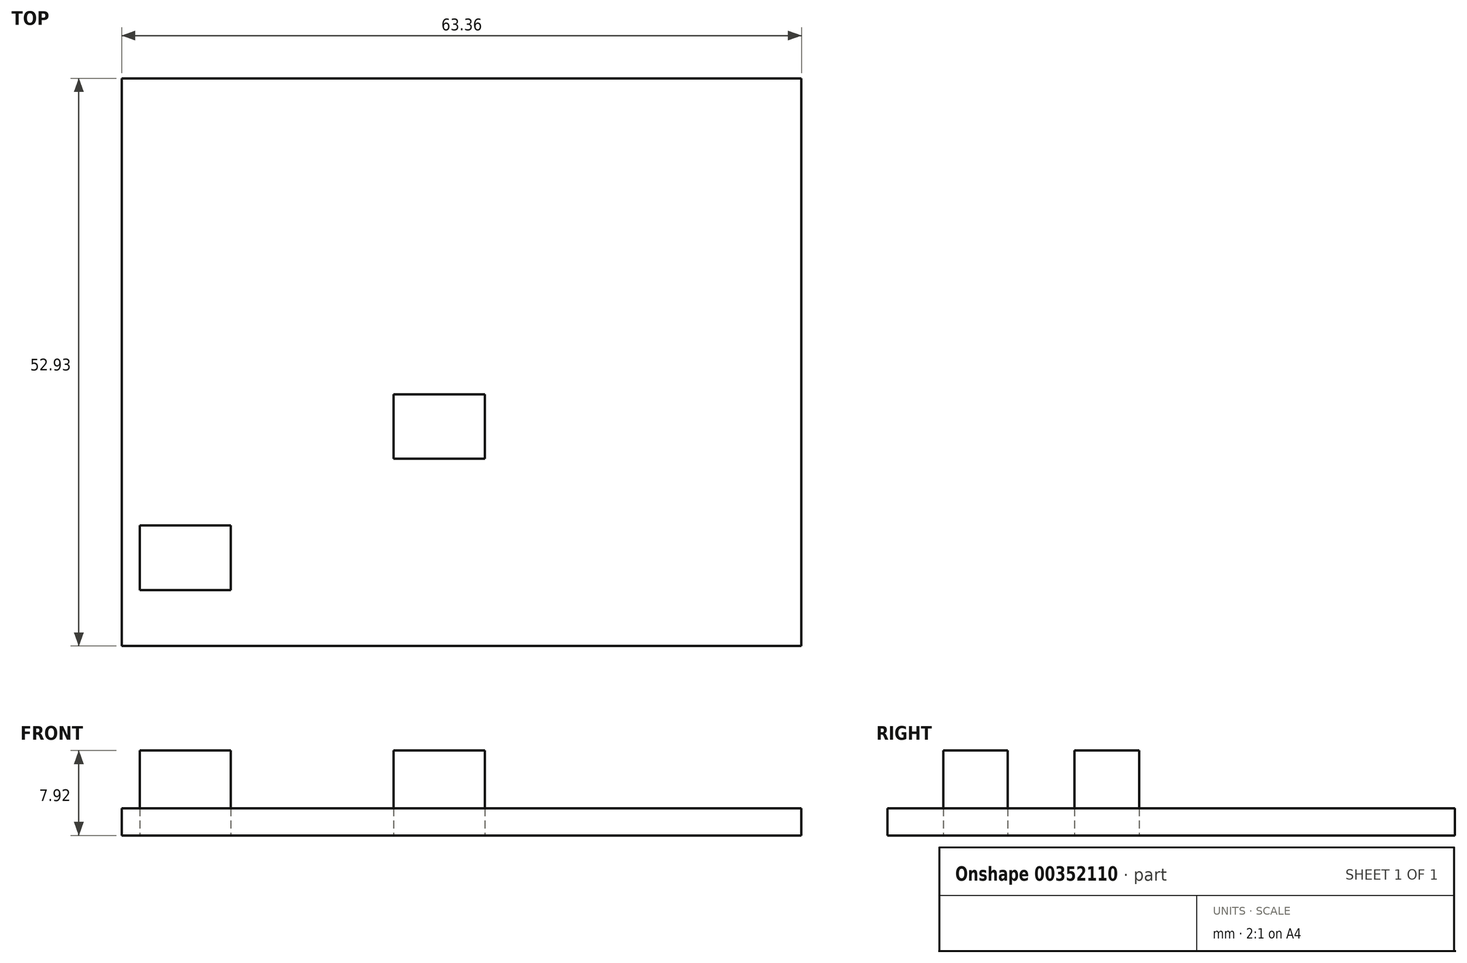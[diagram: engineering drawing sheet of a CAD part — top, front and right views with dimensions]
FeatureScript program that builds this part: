
annotation { "Feature Type Name" : "Feature", "Feature Type Description" : "" }
export const myFeature = defineFeature(function(context is Context, id is Id, definition is map)
    precondition{}
    {
        {
            var Q0;
            Q0=qCreatedBy(makeId("Top.planeOp"),FACE);
            var sketch = newSketch(context, id + "F0", { "sketchPlane" : qUnion([Q0])});
            skLineSegment(sketch, "E0.bottom", {"start": v(-30.08, 24.8) * mm, "end": v(33.28, 24.8) * mm});
            skLineSegment(sketch, "E0.top", {"start": v(-30.08, -28.12) * mm, "end": v(33.28, -28.12) * mm});
            skLineSegment(sketch, "E0.left", {"start": v(-30.08, 24.8) * mm, "end": v(-30.08, -28.12) * mm});
            skLineSegment(sketch, "E0.right", {"start": v(33.28, 24.8) * mm, "end": v(33.28, -28.12) * mm});
            skSolve(sketch);
        }
        {
            var Q0;
            Q0=qSketchRegion(id+"F0",true);
            extrude(context, id + "F1", {"entities" : qUnion([Q0]), "depth" : 2.54 * mm});
        }
        {
            var Q0;
            Q0=qCreatedBy(makeId("Top.planeOp"),FACE);
            var sketch = newSketch(context, id + "F2", { "sketchPlane" : qUnion([Q0])});
            skLineSegment(sketch, "E1.bottom", {"start": v(-28.4, -16.88) * mm, "end": v(-19.9, -16.88) * mm});
            skLineSegment(sketch, "E1.top", {"start": v(-28.4, -22.9) * mm, "end": v(-19.9, -22.9) * mm});
            skLineSegment(sketch, "E1.left", {"start": v(-28.4, -16.88) * mm, "end": v(-28.4, -22.9) * mm});
            skLineSegment(sketch, "E1.right", {"start": v(-19.9, -16.88) * mm, "end": v(-19.9, -22.9) * mm});
            skLineSegment(sketch, "E2.bottom", {"start": v(-4.75, -4.65) * mm, "end": v(3.76, -4.65) * mm});
            skLineSegment(sketch, "E2.top", {"start": v(-4.75, -10.67) * mm, "end": v(3.76, -10.67) * mm});
            skLineSegment(sketch, "E2.left", {"start": v(-4.75, -4.65) * mm, "end": v(-4.75, -10.67) * mm});
            skLineSegment(sketch, "E2.right", {"start": v(3.76, -4.65) * mm, "end": v(3.76, -10.67) * mm});
            skSolve(sketch);
        }
        {
            var Q0;
            Q0=qSketchRegion(id+"F2",true);
            extrude(context, id + "F3", {"entities" : qUnion([Q0]), "depth" : 7.92 * mm});
        }
        {
            var Q0;
            Q0=qCreatedBy(makeId("Front.planeOp"),FACE);
            var sketch = newSketch(context, id + "F4", { "sketchPlane" : qUnion([Q0])});
            skLineSegment(sketch, "E3.bottom", {"start": v(-30.15, 16.17) * mm, "end": v(-28.4, 16.17) * mm});
            skLineSegment(sketch, "E3.top", {"start": v(-30.15, 0) * mm, "end": v(-28.4, 0) * mm});
            skLineSegment(sketch, "E3.left", {"start": v(-30.15, 16.17) * mm, "end": v(-30.15, 0) * mm});
            skLineSegment(sketch, "E3.right", {"start": v(-28.4, 16.17) * mm, "end": v(-28.4, 0) * mm});
            skLineSegment(sketch, "E4.bottom", {"start": v(31.54, 16.17) * mm, "end": v(33.29, 16.17) * mm});
            skLineSegment(sketch, "E4.top", {"start": v(31.54, 0) * mm, "end": v(33.29, 0) * mm});
            skLineSegment(sketch, "E4.left", {"start": v(31.54, 16.17) * mm, "end": v(31.54, 0) * mm});
            skLineSegment(sketch, "E4.right", {"start": v(33.29, 16.17) * mm, "end": v(33.29, 0) * mm});
            skSolve(sketch);
        }
        {
            var Q0;
            Q0=sQuery(id+"F4.wireOp",EDGE,"E3.right");
            var Q1;
            Q1=sQuery(id+"F4.wireOp",EDGE,"E4.left");
            var Q2;
            Q2=sQuery(id+"F4.wireOp",EDGE,"E4.right");
            var Q3;
            Q3=sQuery(id+"F4.wireOp",EDGE,"E3.left");
            var Q4;
            Q4=sQuery(id+"F4.wireOp",EDGE,"E4.top");
            var Q5;
            Q5=sQuery(id+"F4.wireOp",EDGE,"E4.bottom");
            var Q6;
            Q6=sQuery(id+"F4.wireOp",EDGE,"E3.bottom");
            var Q7;
            Q7=sQuery(id+"F4.wireOp",EDGE,"E3.top");
            extrude(context, id + "F5", {"bodyType" : ToolBodyType.SURFACE, "surfaceEntities" : qUnion([Q0, Q1, Q2, Q3, Q4, Q5, Q6, Q7]), "depth" : 27.94 * mm, "hasSecondDirection" : true, "secondDirectionOppositeDirection" : true, "secondDirectionDepth" : 24.64 * mm});
        }
    });
